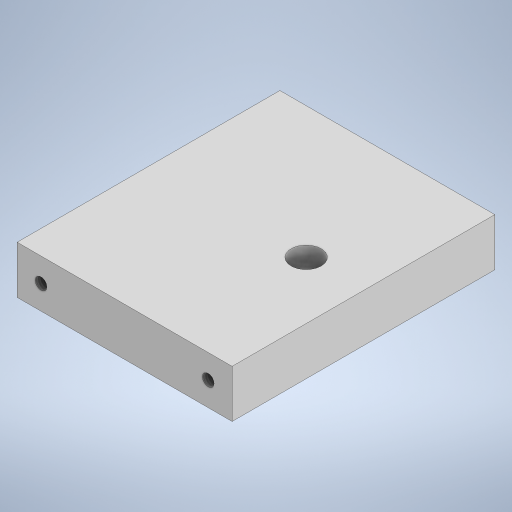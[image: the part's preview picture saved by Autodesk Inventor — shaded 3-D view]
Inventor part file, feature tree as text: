
AUTODESK INVENTOR PART (.ipt)
format: ipt  version: 2024.3 (Build 283343010, 343A)  size: 222,208 bytes
history: native  units: mm
features: sketch x4, hole x3, other x1, extrude x1, projected_geometry x1
ambient origin geometry x8: Origin, YZ Plane, XZ Plane, XY Plane, X Axis, Y Axis, Z Axis, Center Point
bodies: Body1 (feature_tree)
feature tree (10):
  other  "ソリッド1"
  extrude  "押し出し1"  Depth=45.0mm
  hole  "穴1"  [1 undecoded]
  hole  "穴2"  [1 undecoded]
  hole  "穴3"  [1 undecoded]
  sketch  "スケッチ1"
  sketch  "スケッチ2"
  sketch  "スケッチ3"
  projected_geometry  "投影ループ1"
  sketch  "スケッチ4"
note: 3 required parameter values undecoded (feature->parameter linkage not recoverable at this tier; creation-order binding heuristic only, values carry confidence <= 0.55)
